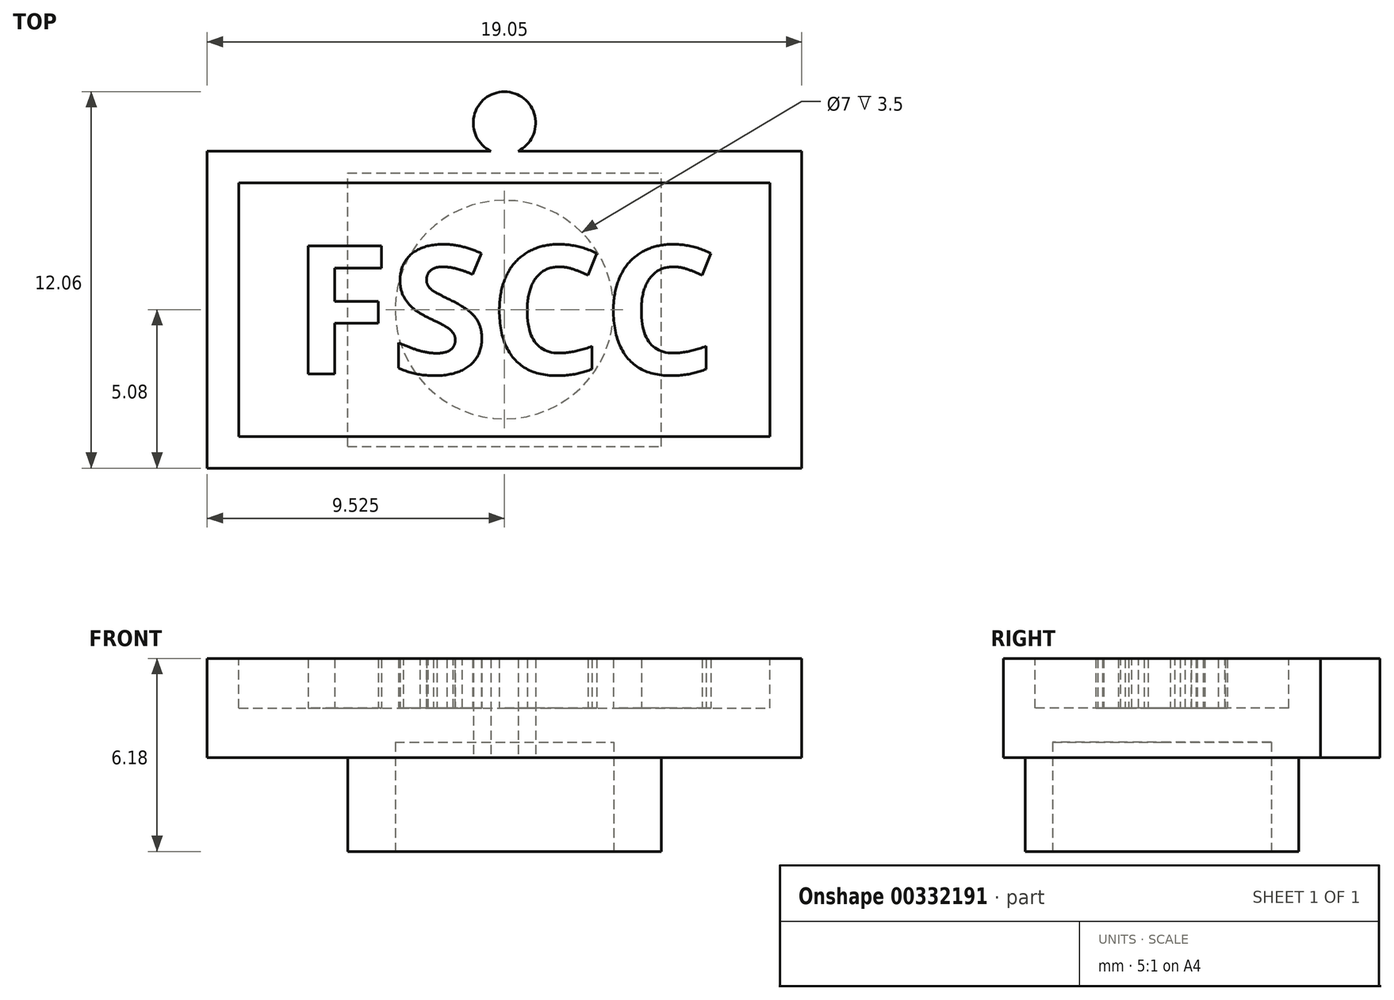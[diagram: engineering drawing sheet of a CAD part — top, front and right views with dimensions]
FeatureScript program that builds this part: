
annotation { "Feature Type Name" : "Feature", "Feature Type Description" : "" }
export const myFeature = defineFeature(function(context is Context, id is Id, definition is map)
    precondition{}
    {
        {
            var Q0;
            Q0=qCreatedBy(makeId("Top.planeOp"),FACE);
            var sketch = newSketch(context, id + "F0", { "sketchPlane" : qUnion([Q0])});
            skLineSegment(sketch, "E0.bottom", {"start": v(-19.05, 10.16) * mm, "end": v(0, 10.16) * mm});
            skLineSegment(sketch, "E0.top", {"start": v(-19.05, 0) * mm, "end": v(0, 0) * mm});
            skLineSegment(sketch, "E0.left", {"start": v(-19.05, 10.16) * mm, "end": v(-19.05, 0) * mm});
            skLineSegment(sketch, "E0.right", {"start": v(0, 10.16) * mm, "end": v(0, 0) * mm});
            skCircle(sketch, "E1", {"center": v(-9.53, 11.06) * mm, "radius": 1 * mm});
            skLineSegment(sketch, "E2", {"start": v(-9.52, 10.16) * mm, "end": v(-9.52, 0) * mm, "construction": true});
            skSolve(sketch);
        }
        {
            var Q0;
            Q0=qSketchRegion(id+"F0",true);
            extrude(context, id + "F1", {"entities" : qUnion([Q0]), "depth" : 3.17 * mm});
        }
        {
            var Q0;
            Q0=makeQuery(id+"F1.opExtrude","CAP_FACE",FACE,{"disambiguationData":[OSD([sQuery(id+"F0.wireOp",EDGE,"E0.bottom"),sQuery(id+"F0.wireOp",EDGE,"E0.top"),sQuery(id+"F0.wireOp",EDGE,"E0.left"),sQuery(id+"F0.wireOp",EDGE,"E0.right")])],"isStart":false});
            var sketch = newSketch(context, id + "F2", { "sketchPlane" : qUnion([Q0])});
            skLineSegment(sketch, "E3.bottom", {"start": v(-18.03, 9.14) * mm, "end": v(-1.02, 9.14) * mm});
            skLineSegment(sketch, "E3.top", {"start": v(-18.03, 1.02) * mm, "end": v(-1.02, 1.02) * mm});
            skLineSegment(sketch, "E3.left", {"start": v(-18.03, 9.14) * mm, "end": v(-18.03, 1.02) * mm});
            skLineSegment(sketch, "E3.right", {"start": v(-1.02, 9.14) * mm, "end": v(-1.02, 1.02) * mm});
            skSolve(sketch);
        }
        {
            var Q0;
            Q0=qSketchRegion(id+"F2",true);
            extrude(context, id + "F3", {"entities" : qUnion([Q0]), "operationType" : NewBodyOperationType.REMOVE, "oppositeDirection" : true, "depth" : 1.59 * mm});
        }
        {
            var Q0;
            Q0=makeQuery(id+"F1.opExtrude","CAP_FACE",FACE,{"disambiguationData":[OSD([sQuery(id+"F0.wireOp",EDGE,"E0.bottom"),sQuery(id+"F0.wireOp",EDGE,"E0.top"),sQuery(id+"F0.wireOp",EDGE,"E0.left"),sQuery(id+"F0.wireOp",EDGE,"E0.right"),sQuery(id+"F0.wireOp",EDGE,"E1"),sQuery(id+"F0.wireOp",EDGE,"25aa8db4-dd9b-41d2-b8c9-1594e9b75191"),sQuery(id+"F0.wireOp",EDGE,"40f63cb3-13d8-4821-a3c4-c05e674bd89b0.MirrorC")])],"isStart":true});
            var sketch = newSketch(context, id + "F4", { "sketchPlane" : qUnion([Q0])});
            skLineSegment(sketch, "E4.bottom", {"start": v(-14.55, -0.7) * mm, "end": v(-4.5, -0.7) * mm});
            skLineSegment(sketch, "E4.top", {"start": v(-14.55, -9.46) * mm, "end": v(-4.5, -9.46) * mm});
            skLineSegment(sketch, "E4.left", {"start": v(-14.55, -0.7) * mm, "end": v(-14.55, -9.46) * mm});
            skLineSegment(sketch, "E4.right", {"start": v(-4.5, -0.7) * mm, "end": v(-4.5, -9.46) * mm});
            skSolve(sketch);
        }
        {
            var Q0;
            Q0=qSketchRegion(id+"F4",true);
            extrude(context, id + "F5", {"entities" : qUnion([Q0]), "operationType" : NewBodyOperationType.ADD, "depth" : 3 * mm, "offsetDistance" : 25 * mm});
        }
        {
            var Q0;
            Q0=makeQuery(id+"F5.opExtrude","CAP_FACE",FACE,{"disambiguationData":[OSD([sQuery(id+"F4.wireOp",EDGE,"E4.bottom"),sQuery(id+"F4.wireOp",EDGE,"E4.top"),sQuery(id+"F4.wireOp",EDGE,"E4.left"),sQuery(id+"F4.wireOp",EDGE,"E4.right")])],"isStart":false});
            var sketch = newSketch(context, id + "F6", { "sketchPlane" : qUnion([Q0])});
            skCircle(sketch, "E5", {"center": v(-9.52, -5.08) * mm, "radius": 3.5 * mm});
            skLineSegment(sketch, "E6", {"start": v(-19.05, -5.08) * mm, "end": v(0, -5.08) * mm, "construction": true});
            skPoint(sketch, "E6.endSnap0", {"position": v(-4.5, -5.08) * mm});
            skLineSegment(sketch, "E7", {"start": v(-9.53, 0) * mm, "end": v(-9.53, -9.46) * mm, "construction": true});
            skSolve(sketch);
        }
        {
            var Q0;
            Q0=makeQuery(id+"F6.imprint","IMPRINT",FACE,{"disambiguationData":[TD([[makeQuery(id+"F6.imprint","IMPRINT",EDGE,{"derivedFrom":sQuery(id+"F6.wireOp",EDGE,"E5")}),1.0]])]});
            extrude(context, id + "F7", {"entities" : qUnion([Q0]), "operationType" : NewBodyOperationType.REMOVE, "oppositeDirection" : true, "depth" : 3.5 * mm, "offsetDistance" : 25 * mm});
        }
        {
            var Q0;
            Q0=makeQuery(id+"F3.boolean.opBoolean","COPY",FACE,{"derivedFrom":makeQuery(id+"F3.opExtrude","CAP_FACE",FACE,{"disambiguationData":[OSD([sQuery(id+"F2.wireOp",EDGE,"E3.bottom"),sQuery(id+"F2.wireOp",EDGE,"E3.top"),sQuery(id+"F2.wireOp",EDGE,"E3.left"),sQuery(id+"F2.wireOp",EDGE,"E3.right")])],"isStart":false})});
            var sketch = newSketch(context, id + "F8", { "sketchPlane" : qUnion([Q0])});
            skText(sketch, "E8", { "text": "FSCC", "fontName": "OpenSans-Bold.ttf"});
            const initialGuessF8  = {"E8": [-0.01633, 0.00302, 1, 0, 0.00413]};
            skSetInitialGuess(sketch, initialGuessF8);
            skSolve(sketch);
        }
        {
            var Q0;
            Q0 = qSketchRegion(id + "F8", true);
            var Q1;
            Q1=makeQuery(id+"F1.opExtrude","CAP_FACE",FACE,{"disambiguationData":[OSD([sQuery(id+"F0.wireOp",EDGE,"E0.bottom"),sQuery(id+"F0.wireOp",EDGE,"E0.top"),sQuery(id+"F0.wireOp",EDGE,"E0.left"),sQuery(id+"F0.wireOp",EDGE,"E0.right"),sQuery(id+"F0.wireOp",EDGE,"E1")])],"isStart":false});
            extrude(context, id + "F9", {"entities" : qUnion([Q0]), "operationType" : NewBodyOperationType.ADD, "endBound" : BoundingType.UP_TO_SURFACE, "depth" : 25 * mm, "endBoundEntityFace" : qUnion([Q1]), "offsetDistance" : 25 * mm});
        }
    });
